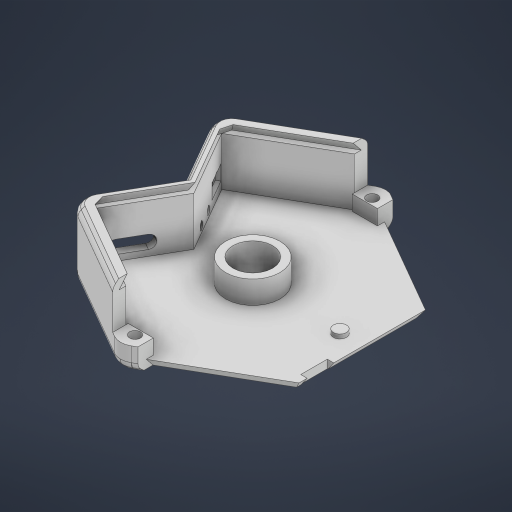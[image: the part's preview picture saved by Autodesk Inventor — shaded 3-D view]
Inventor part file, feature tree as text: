
AUTODESK INVENTOR PART (.ipt)
format: ipt  version: 2023 (Build 270158000, 158)  size: 782,336 bytes
history: native  units: in
note: dims shown in document units (in); Inventor stores cm internally (conversion verified against a paired STEP export)
features: extrude x28, sketch x17, move_body x8, direct_edit x6, draft x5, fillet x2, plane x1, chamfer x1
ambient origin geometry x8: Origin, YZ Plane, XZ Plane, XY Plane, X Axis, Y Axis, Z Axis, Center Point
bodies: Solid1 (feature_tree)
feature tree (68):
  sketch  "Sketch1"  dims[d0=1.939in d1=0.5157in]
  extrude  "Extrusion1"  Depth=0.5157in
  extrude  "Extrusion2"  Depth=0.4449in
  extrude  "Extrusion3"  Depth=0.0728in
  extrude  "Extrusion4"  Depth=0.0787in TaperAngle=0.0deg
  extrude  "Extrusion5"  Depth=0.6181in TaperAngle=0.0deg
  extrude  "Extrusion6"  Depth=0.1122in
  direct_edit  "Direct Edit1"
  extrude  "Extrusion9"  TaperAngle=0.0deg  [1 undecoded]
  extrude  "Extrusion10"  Depth=0.3307in TaperAngle=0.0deg
  extrude  "Extrusion11"  Depth=0.113in
  extrude  "Extrusion12"  Depth=0.2276in
  extrude  "Extrusion13"  TaperAngle=0.0deg  [1 undecoded]
  extrude  "Extrusion14"  Depth=0.1929in
  extrude  "Extrusion15"  Depth=0.185in
  extrude  "Extrusion16"  Depth=0.0689in
  direct_edit  "Direct Edit2"
  direct_edit  "Direct Edit3"
  sketch  "Sketch13"  dims[d21=0.176in d22=0.113in]
  extrude  "Extrusion17"  Depth=0.6871in
  sketch  "Sketch14"  dims[d23=0.1142in d24=0.2276in]
  extrude  "Extrusion19"  TaperAngle=0.0deg  [1 undecoded]
  sketch  "Sketch18"  dims[d25=0.1142in d26=0.0in d27=0.0in]
  extrude  "Extrusion26"  Depth=0.0787in TaperAngle=0.0deg
  extrude  "Extrusion27"  Depth=0.3937in TaperAngle=0.0deg
  sketch  "Sketch19"  dims[d33=0.0in d34=0.0in d35=-0.0728in d38=0.1929in]
  extrude  "Extrusion28"  TaperAngle=0.0deg  [1 undecoded]
  extrude  "Extrusion29"  Depth=0.3937in TaperAngle=0.0deg
  draft  "FaceDraft1"
  draft  "FaceDraft2"
  draft  "FaceDraft4"
  sketch  "Sketch20"  dims[d39=0.0591in d40=0.185in]
  extrude  "Extrusion30"  Depth=0.0787in TaperAngle=0.0deg
  extrude  "Extrusion31"  Depth=0.0787in
  extrude  "Extrusion32"  Depth=0.0787in
  direct_edit  "Direct Edit5"
  plane  "Work Plane1"
  sketch  "Sketch22"  dims[d43=0.0689in d44=0.6871in]
  extrude  "Extrusion37"  Depth=0.0787in TaperAngle=0.0deg
  extrude  "Extrusion38"  Depth=0.0787in
  extrude  "Extrusion39"  Depth=0.0787in TaperAngle=0.0deg
  extrude  "Extrusion40"  Depth=0.0787in TaperAngle=0.0deg
  extrude  "Extrusion42"  TaperAngle=0.0deg  [1 undecoded]
  draft  "FaceDraft5"
  fillet  "Fillet1"  Radius=0.2405in
  draft  "FaceDraft6"
  chamfer  "Chamfer5"  Distance=0.0787in
  fillet  "Fillet5"  [1 undecoded]
  direct_edit  "Direct Edit8"
  direct_edit  "Direct Edit9"
  sketch  "Sketch2"  dims[d2=0.374in d3=0.4449in]
  sketch  "Sketch3"  dims[d4=0.0295in d5=0.0728in]
  sketch  "Sketch4"  dims[d6=0.1378in d7=0.0787in d8=0.0in]
  sketch  "Sketch7"  dims[d9=0.2953in d10=0.0in d11=0.6181in d12=0.0in]
  sketch  "Sketch8"  dims[d13=0.2087in d14=0.1122in]
  sketch  "Sketch9"  dims[d15=0.1673in d16=0.0in d17=0.0in]
  sketch  "Sketch11"  dims[d18=0.0394in d19=0.3307in d20=0.0in]
  sketch  "Sketch21"  dims[d41=0.0591in d42=0.0689in]
  sketch  "Sketch23"  dims[d45=0.6871in d46=0.0in d47=0.0in]
  sketch  "Sketch24"  dims[d48=0.2953in d49=0.0787in d50=0.0in d51=0.3937in d52=0.0in d56=0.0in d57=0.0in d58=0.3937in d59=0.0in d60=0.3976in d61=0.0in d62=0.0315in d63=0.0787in d64=0.0689in d65=0.0in d66=0.0787in d67=0.0689in d68=0.0in d69=0.0in d70=0.0in d71=0.0787in d72=0.0in d73=0.0in d74=-0.0689in d78=0.2405in d80=0.0787in d81=0.0in d82=0.0in d85=0.2405in d86=0.0787in d87=0.0in d88=0.0in d116=30.0deg d117=0.0787in d118=0.0in d119=0.0in d120=0.3937in d121=0.0in d122=0.0787in d123=30.0deg d124=0.0in d125=0.0in d126=0.3937in d127=0.0in d128=0.2405in d129=-0.2405in d131=0.0in d132=0.0in d133=0.0787in d134=0.2405in d135=0.1614in d137=0.063in d138=0.0in d139=0.0709in d140=0.0in d141=0.0787in d142=0.0in d144=120.0deg d145=0.0in d146=0.0in d147=0.0157in d148=0.1575in d154=90.0deg d155=0.1921in d156=0.2953in d157=0.2028in d160=0.1354in d161=0.1535in d179=0.126in d180=0.8268in d181=0.0394in d182=0.0in d183=0.126in d184=0.126in d185=0.3937in d186=0.0in d199=0.0in d200=0.0in d201=0.1417in d202=0.0984in d204=0.0394in d205=0.0in d207=120.0deg d210=45.0deg d211=0.0in d212=0.0in d213=-0.2405in d214=-0.2405in d215=0.0492in d216=0.0787in d217=45.0deg d218=0.0787in d219=0.0157in d220=0.0118in d221=0.0in d222=0.0in d223=-0.0059in d224=0.1043in d226=0.0906in d228=0.0in d229=0.0in d230=0.0197in d231=0.0in d232=0.0in d233=-0.0197in d234=0.1535in d235=0.0079in d236=0.1535in d237=0.0906in d239=0.1043in d240=0.0079in d36=0.0344in d112=0.0197in d113=0.0344in d114=0.0197in d115=0.0344in d136=0.0344in d166=0.0197in d167=0.0344in d168=0.0197in d169=0.0344in d225=0.0197in d227=0.0197in]
  move_body  "Move1"
  move_body  "Move2"
  move_body  "Move3"
  move_body  "Move8"
  move_body  "Move9"
  move_body  "Move15"
  move_body  "Move16"
  move_body  "Move17"
note: 6 required parameter values undecoded (feature->parameter linkage not recoverable at this tier; creation-order binding heuristic only, values carry confidence <= 0.55)
